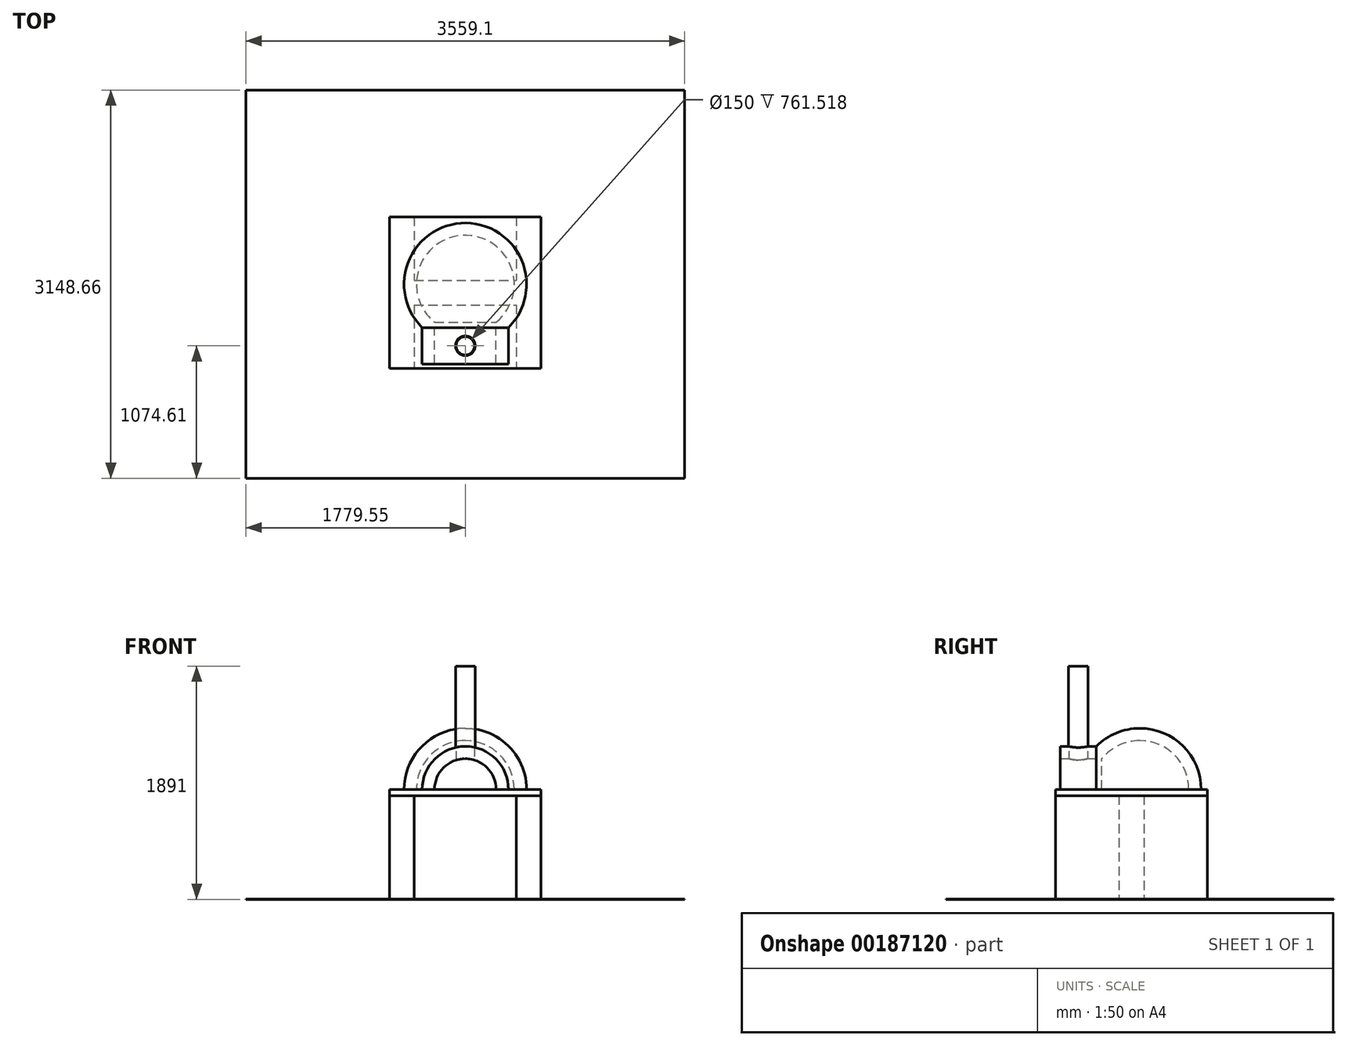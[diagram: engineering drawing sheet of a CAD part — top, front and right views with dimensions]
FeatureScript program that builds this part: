
annotation { "Feature Type Name" : "Feature", "Feature Type Description" : "" }
export const myFeature = defineFeature(function(context is Context, id is Id, definition is map)
    precondition{}
    {
        {
            assignVariable(context, id + "F0", {"name" : "BlockHeight", "anyValue" : 200});
        }
        {
            assignVariable(context, id + "F1", {"name" : "PlateThickness", "anyValue" : 50});
        }
        {
            assignVariable(context, id + "F2", {"name" : "BaseHeight", "anyValue" : ((getVariable(context, 'BlockHeight') + 10) * 4) + getVariable(context, 'PlateThickness')});
        }
        {
            var Q0;
            Q0=qCreatedBy(makeId("Top.planeOp"),FACE);
            cPlane(context, id + "F3", {"entities" : qUnion([Q0]), "cplaneType" : CPlaneType.OFFSET, "offset" : (getVariable(context, 'BaseHeight')) * mm, "width" : 150 * mm, "height" : 150 * mm});
        }
        {
            assignVariable(context, id + "F4", {"name" : "ChannelRadius", "anyValue" : 250});
        }
        {
            assignVariable(context, id + "F5", {"name" : "OvenRadius", "anyValue" : getVariable(context, 'ChannelRadius') / 0.63});
        }
        {
            assignVariable(context, id + "F6", {"name" : "WallThickness", "anyValue" : 100});
        }
        {
            assignVariable(context, id + "F7", {"name" : "ChannelLength", "anyValue" : 150});
        }
        {
            assignVariable(context, id + "F8", {"name" : "ChimneyHeight", "anyValue" : 1000});
        }
        {
            var Q0;
            Q0=qCreatedBy(makeId("Front.planeOp"),FACE);
            var sketch = newSketch(context, id + "F9", { "sketchPlane" : qUnion([Q0])});
            skLineSegment(sketch, "E0", {"start": v(0, 0) * mm, "end": v(0, 2075.89) * mm, "construction": true});
            skLineSegment(sketch, "E1", {"start": v(-818.6, 890) * mm, "end": v(396.83, 890) * mm, "construction": true});
            skArc(sketch, "E2", {"start": v(-396.83, 890) * mm, "mid": v(-280.6, 1170.6) * mm, "end": v(0, 1286.83) * mm});
            skArc(sketch, "E3.0", {"start": v(-496.83, 890) * mm, "mid": v(-351.3, 1241.3) * mm, "end": v(0, 1386.83) * mm});
            skLineSegment(sketch, "E4", {"start": v(-496.83, 890) * mm, "end": v(-396.83, 890) * mm});
            skLineSegment(sketch, "E5", {"start": v(396.83, 890) * mm, "end": v(496.83, 890) * mm});
            skLineSegment(sketch, "E6", {"start": v(0, 1386.83) * mm, "end": v(0, 1286.83) * mm});
            skLineSegment(sketch, "E7.trimOffspring", {"start": v(496.83, 890) * mm, "end": v(884.66, 890) * mm, "construction": true});
            skSolve(sketch);
        }
        {
            var Q0;
            Q0 = qSketchRegion(id + "F9", true);
            var Q1;
            Q1=sQuery(id+"F9.wireOp",EDGE,"E0");
            revolve(context, id + "F10", {"entities" : qUnion([Q0]), "axis" : qUnion([Q1]), "revolveType" : RevolveType.FULL});
        }
        {
            var Q0;
            Q0=qCreatedBy(makeId("Front.planeOp"),FACE);
            var sketch = newSketch(context, id + "F11", { "sketchPlane" : qUnion([Q0])});
            skLineSegment(sketch, "E8", {"start": v(0, 0) * mm, "end": v(0, 1807.97) * mm, "construction": true});
            skLineSegment(sketch, "E9", {"start": v(-977.33, 890) * mm, "end": v(1069.97, 890) * mm, "construction": true});
            skArc(sketch, "E10", {"start": v(-250, 890) * mm, "mid": v(0, 1140) * mm, "end": v(250, 890) * mm});
            skLineSegment(sketch, "E11", {"start": v(-250, 890) * mm, "end": v(250, 890) * mm});
            skSolve(sketch);
        }
        {
            var Q0;
            Q0 = qSketchRegion(id + "F11", true);
            extrude(context, id + "F12", {"entities" : qUnion([Q0]), "operationType" : NewBodyOperationType.REMOVE, "endBound" : BoundingType.THROUGH_ALL, "depth" : 25 * mm});
        }
        {
            var Q0;
            Q0=qCreatedBy(makeId("Front.planeOp"),FACE);
            cPlane(context, id + "F13", {"entities" : qUnion([Q0]), "cplaneType" : CPlaneType.OFFSET, "offset" : (getVariable(context, 'OvenRadius') + getVariable(context, 'WallThickness') + getVariable(context, 'ChannelLength')) * mm, "width" : 150 * mm, "height" : 150 * mm});
        }
        {
            var Q0;
            Q0=qCreatedBy(id+"F13.planeOp",FACE);
            var sketch = newSketch(context, id + "F14", { "sketchPlane" : qUnion([Q0])});
            skArc(sketch, "E12", {"start": v(-250, 890) * mm, "mid": v(0, 1140) * mm, "end": v(250, 890) * mm});
            skArc(sketch, "E13.0", {"start": v(250, 890) * mm, "mid": v(0, 1140) * mm, "end": v(-250, 890) * mm, "construction": true});
            skLineSegment(sketch, "E14.0", {"start": v(496.83, 890) * mm, "end": v(-496.83, 890) * mm, "construction": true});
            skArc(sketch, "E15.0", {"start": v(350, 890) * mm, "mid": v(0, 1240) * mm, "end": v(-350, 890) * mm});
            skLineSegment(sketch, "E16", {"start": v(-350, 890) * mm, "end": v(-250, 890) * mm});
            skLineSegment(sketch, "E17", {"start": v(250, 890) * mm, "end": v(350, 890) * mm});
            skSolve(sketch);
        }
        {
            var Q0;
            Q0 = qSketchRegion(id + "F14", true);
            var Q1;
            Q1=makeQuery(id+"F10.opRevolve","SWEPT_FACE",FACE,{"disambiguationData":[OSD([sQuery(id+"F9.wireOp",EDGE,"E3.0")])]});
            extrude(context, id + "F15", {"entities" : qUnion([Q0]), "operationType" : NewBodyOperationType.ADD, "endBound" : BoundingType.UP_TO_SURFACE, "oppositeDirection" : true, "endBoundEntityFace" : qUnion([Q1]), "depth" : 25 * mm});
        }
        {
            var Q0;
            Q0=qCreatedBy(id+"F3.planeOp",FACE);
            var sketch = newSketch(context, id + "F16", { "sketchPlane" : qUnion([Q0])});
            skLineSegment(sketch, "E18", {"start": v(0, 0) * mm, "end": v(0, -1179.22) * mm, "construction": true});
            skLineSegment(sketch, "E19.0", {"start": v(-350, -352.61) * mm, "end": v(350, -352.61) * mm, "construction": true});
            skLineSegment(sketch, "E20.0", {"start": v(350, -646.83) * mm, "end": v(-350, -646.83) * mm, "construction": true});
            skLineSegment(sketch, "E21", {"start": v(-583.06, -499.72) * mm, "end": v(587.56, -499.72) * mm, "construction": true});
            skCircle(sketch, "E22", {"center": v(0, -499.72) * mm, "radius": 75 * mm});
            skSolve(sketch);
        }
        {
            var Q0;
            Q0 = qSketchRegion(id + "F16", true);
            var Q1;
            Q1=makeQuery(id+"F15.opExtrude","SWEPT_FACE",FACE,{"disambiguationData":[OSD([sQuery(id+"F14.wireOp",EDGE,"E15.0")])]});
            extrude(context, id + "F17", {"entities" : qUnion([Q0]), "operationType" : NewBodyOperationType.REMOVE, "endBound" : BoundingType.UP_TO_SURFACE, "endBoundEntityFace" : qUnion([Q1]), "depth" : 25 * mm});
        }
        {
            var Q0;
            Q0=qCreatedBy(id+"F3.planeOp",FACE);
            cPlane(context, id + "F18", {"entities" : qUnion([Q0]), "cplaneType" : CPlaneType.OFFSET, "offset" : (getVariable(context, 'ChimneyHeight')) * mm, "width" : 150 * mm, "height" : 150 * mm});
        }
        {
            var Q0;
            Q0=qCreatedBy(id+"F18.planeOp",FACE);
            var sketch = newSketch(context, id + "F19", { "sketchPlane" : qUnion([Q0])});
            skCircle(sketch, "E23", {"center": v(0, -499.72) * mm, "radius": 75 * mm});
            skCircle(sketch, "E24", {"center": v(0, -499.72) * mm, "radius": 80 * mm});
            skSolve(sketch);
        }
        {
            var Q0;
            Q0 = qSketchRegion(id + "F19", true);
            var Q1;
            Q1=makeQuery(id+"F15.opExtrude","SWEPT_FACE",FACE,{"disambiguationData":[OSD([sQuery(id+"F14.wireOp",EDGE,"E15.0")])]});
            extrude(context, id + "F20", {"entities" : qUnion([Q0]), "operationType" : NewBodyOperationType.ADD, "endBound" : BoundingType.UP_TO_SURFACE, "oppositeDirection" : true, "endBoundEntityFace" : qUnion([Q1]), "depth" : 25 * mm});
        }
        {
            var Q0;
            Q0=qCreatedBy(id+"F3.planeOp",FACE);
            var sketch = newSketch(context, id + "F21", { "sketchPlane" : qUnion([Q0])});
            skLineSegment(sketch, "E25.bottom", {"start": v(-615, 546.83) * mm, "end": v(615, 546.83) * mm});
            skLineSegment(sketch, "E25.top", {"start": v(-615, -683.17) * mm, "end": v(615, -683.17) * mm});
            skLineSegment(sketch, "E25.left", {"start": v(-615, 546.83) * mm, "end": v(-615, -683.17) * mm});
            skLineSegment(sketch, "E25.right", {"start": v(615, 546.83) * mm, "end": v(615, -683.17) * mm});
            skLineSegment(sketch, "E26", {"start": v(0, 1106.1) * mm, "end": v(0, -1306.3) * mm, "construction": true});
            skLineSegment(sketch, "E27", {"start": v(-1334.23, 0) * mm, "end": v(1386.65, 0) * mm, "construction": true});
            skLineSegment(sketch, "E28", {"start": v(-1614.36, 496.83) * mm, "end": v(1564.22, 496.83) * mm, "construction": true});
            skSolve(sketch);
        }
        {
            var Q0;
            Q0 = qSketchRegion(id + "F21", true);
            extrude(context, id + "F22", {"entities" : qUnion([Q0]), "oppositeDirection" : true, "depth" : (getVariable(context, 'PlateThickness')) * mm});
        }
        {
            var Q0;
            Q0=qCreatedBy(makeId("Top.planeOp"),FACE);
            var sketch = newSketch(context, id + "F23", { "sketchPlane" : qUnion([Q0])});
            skLineSegment(sketch, "E29.bottom", {"start": v(1779.55, -1574.33) * mm, "end": v(-1779.55, -1574.33) * mm});
            skLineSegment(sketch, "E29.top", {"start": v(1779.55, 1574.33) * mm, "end": v(-1779.55, 1574.33) * mm});
            skLineSegment(sketch, "E29.left", {"start": v(1779.55, -1574.33) * mm, "end": v(1779.55, 1574.33) * mm});
            skLineSegment(sketch, "E29.right", {"start": v(-1779.55, -1574.33) * mm, "end": v(-1779.55, 1574.33) * mm});
            skPoint(sketch, "E29.middle", {"position": v(0, 0) * mm});
            skSolve(sketch);
        }
        {
            var Q0;
            Q0 = qSketchRegion(id + "F23", true);
            extrude(context, id + "F24", {"entities" : qUnion([Q0]), "oppositeDirection" : true, "depth" : 1 * mm});
        }
        {
            var Q0;
            Q0=qCreatedBy(makeId("Top.planeOp"),FACE);
            var sketch = newSketch(context, id + "F25", { "sketchPlane" : qUnion([Q0])});
            skLineSegment(sketch, "E30.bottom", {"start": v(-615, 546.83) * mm, "end": v(-415, 546.83) * mm});
            skLineSegment(sketch, "E30.top", {"start": v(-615, -683.17) * mm, "end": v(-415, -683.17) * mm});
            skLineSegment(sketch, "E30.left", {"start": v(-615, 546.83) * mm, "end": v(-615, -683.17) * mm});
            skLineSegment(sketch, "E30.right", {"start": v(-415, 546.83) * mm, "end": v(-415, 31.83) * mm});
            skLineSegment(sketch, "E31.bottom", {"start": v(415, 546.83) * mm, "end": v(615, 546.83) * mm});
            skLineSegment(sketch, "E31.top", {"start": v(415, -683.17) * mm, "end": v(615, -683.17) * mm});
            skLineSegment(sketch, "E31.left", {"start": v(415, 546.83) * mm, "end": v(415, 31.83) * mm});
            skLineSegment(sketch, "E31.right", {"start": v(615, 546.83) * mm, "end": v(615, -683.17) * mm});
            skLineSegment(sketch, "E32.bottom", {"start": v(-415, 31.83) * mm, "end": v(415, 31.83) * mm});
            skLineSegment(sketch, "E32.top", {"start": v(-415, -168.17) * mm, "end": v(415, -168.17) * mm});
            skLineSegment(sketch, "E33", {"start": v(-1333.05, -68.17) * mm, "end": v(1318.5, -68.17) * mm, "construction": true});
            skLineSegment(sketch, "E34.trimOffspring", {"start": v(415, -168.17) * mm, "end": v(415, -683.17) * mm});
            skLineSegment(sketch, "E35.trimOffspring", {"start": v(-415, -168.17) * mm, "end": v(-415, -683.17) * mm});
            skSolve(sketch);
        }
        {
            var Q0;
            Q0 = qSketchRegion(id + "F25", true);
            extrude(context, id + "F26", {"entities" : qUnion([Q0]), "depth" : (getVariable(context, 'BaseHeight') - getVariable(context, 'PlateThickness')) * mm});
        }
    });
